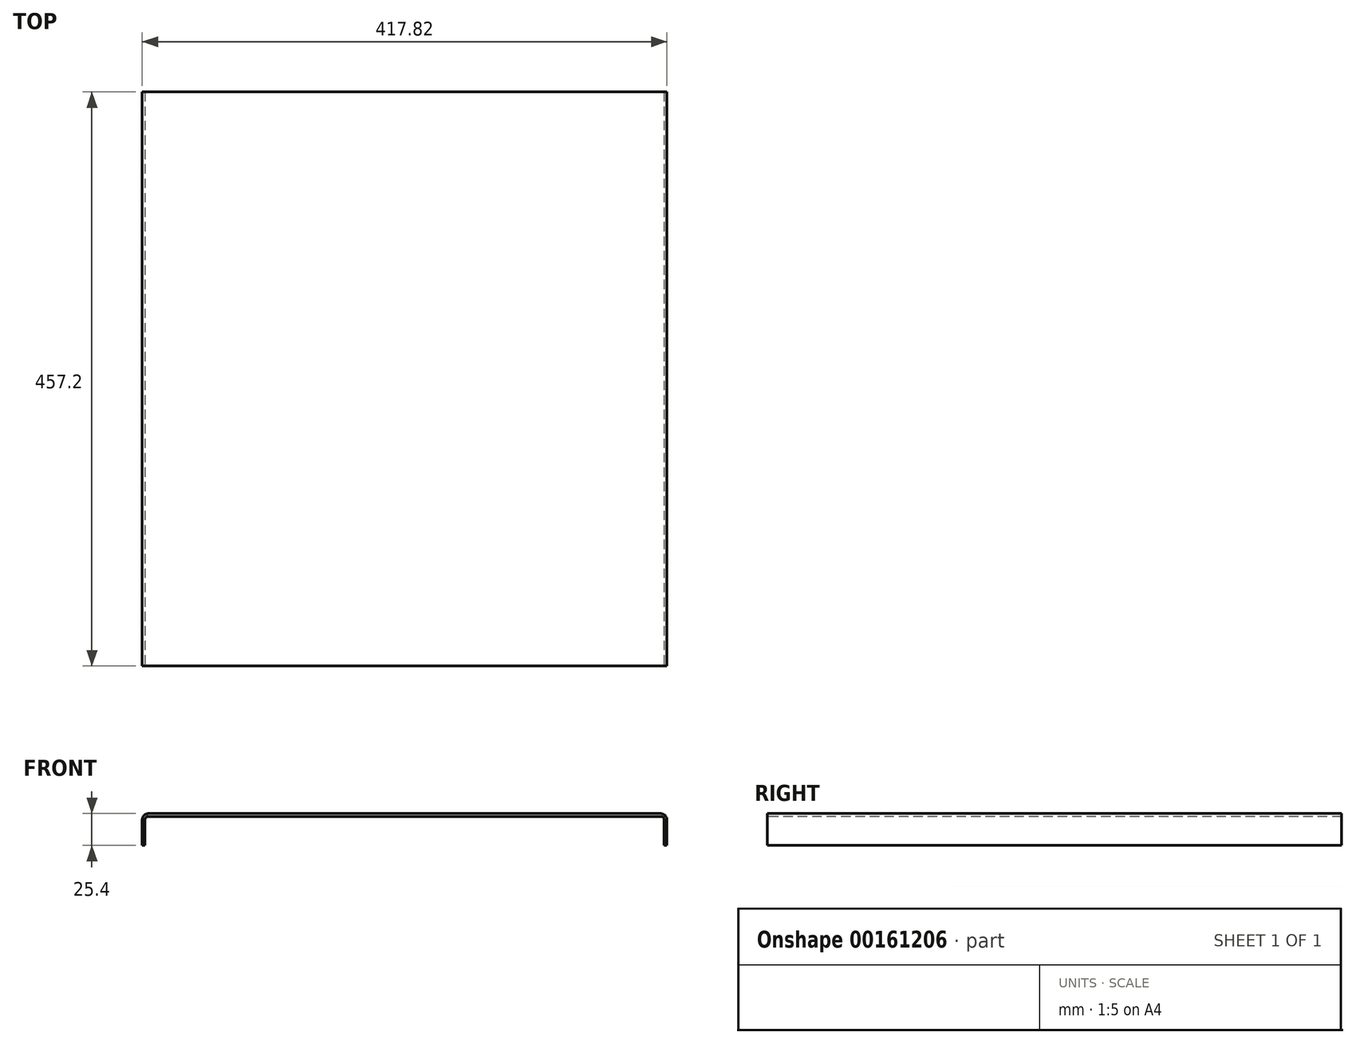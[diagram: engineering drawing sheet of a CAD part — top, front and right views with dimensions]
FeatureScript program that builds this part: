
annotation { "Feature Type Name" : "Feature", "Feature Type Description" : "" }
export const myFeature = defineFeature(function(context is Context, id is Id, definition is map)
    precondition{}
    {
        {
            var Q0;
            Q0=qCreatedBy(makeId("Front.planeOp"),FACE);
            var sketch = newSketch(context, id + "F0", { "sketchPlane" : qUnion([Q0])});
            skLineSegment(sketch, "E0", {"start": v(-203.84, 0) * mm, "end": v(203.84, 0) * mm});
            skLineSegment(sketch, "E1", {"start": v(-208.92, -5.08) * mm, "end": v(-208.92, -25.4) * mm});
            skPoint(sketch, "E2.visualSharp", {"position": v(-208.92, 0) * mm});
            skArc(sketch, "E2.filletArc", {"start": v(-203.84, 0) * mm, "mid": v(-207.43, -1.49) * mm, "end": v(-208.92, -5.08) * mm});
            skLineSegment(sketch, "E3", {"start": v(-204.09, -2.29) * mm, "end": v(204.09, -2.29) * mm});
            skLineSegment(sketch, "E4", {"start": v(-206.63, -25.4) * mm, "end": v(-206.63, -4.83) * mm});
            skPoint(sketch, "E5.orphan", {"position": v(-139.7, -2.29) * mm});
            skPoint(sketch, "E6.visualSharp", {"position": v(-206.63, -2.29) * mm});
            skArc(sketch, "E6.filletArc", {"start": v(-204.09, -2.29) * mm, "mid": v(-205.89, -3.03) * mm, "end": v(-206.63, -4.83) * mm});
            skLineSegment(sketch, "E7", {"start": v(-208.92, -25.4) * mm, "end": v(-206.63, -25.4) * mm});
            skArc(sketch, "E8.MirrorCS", {"start": v(204.09, -2.29) * mm, "mid": v(205.89, -3.03) * mm, "end": v(206.63, -4.83) * mm});
            skArc(sketch, "E9.MirrorCS", {"start": v(203.84, 0) * mm, "mid": v(207.43, -1.49) * mm, "end": v(208.92, -5.08) * mm});
            skLineSegment(sketch, "E10.MirrorCS", {"start": v(208.92, -25.4) * mm, "end": v(206.63, -25.4) * mm});
            skPoint(sketch, "E11.MirrorP", {"position": v(208.92, 0) * mm});
            skLineSegment(sketch, "E12.MirrorCS", {"start": v(208.92, -5.08) * mm, "end": v(208.92, -25.4) * mm});
            skLineSegment(sketch, "E13.MirrorCS", {"start": v(206.63, -25.4) * mm, "end": v(206.63, -4.83) * mm});
            skPoint(sketch, "E14.MirrorP", {"position": v(206.63, -2.29) * mm});
            skSolve(sketch);
        }
        {
            var Q0;
            Q0 = qSketchRegion(id + "F0", true);
            extrude(context, id + "F1", {"entities" : qUnion([Q0]), "oppositeDirection" : true, "depth" : 457.2 * mm});
        }
    });
